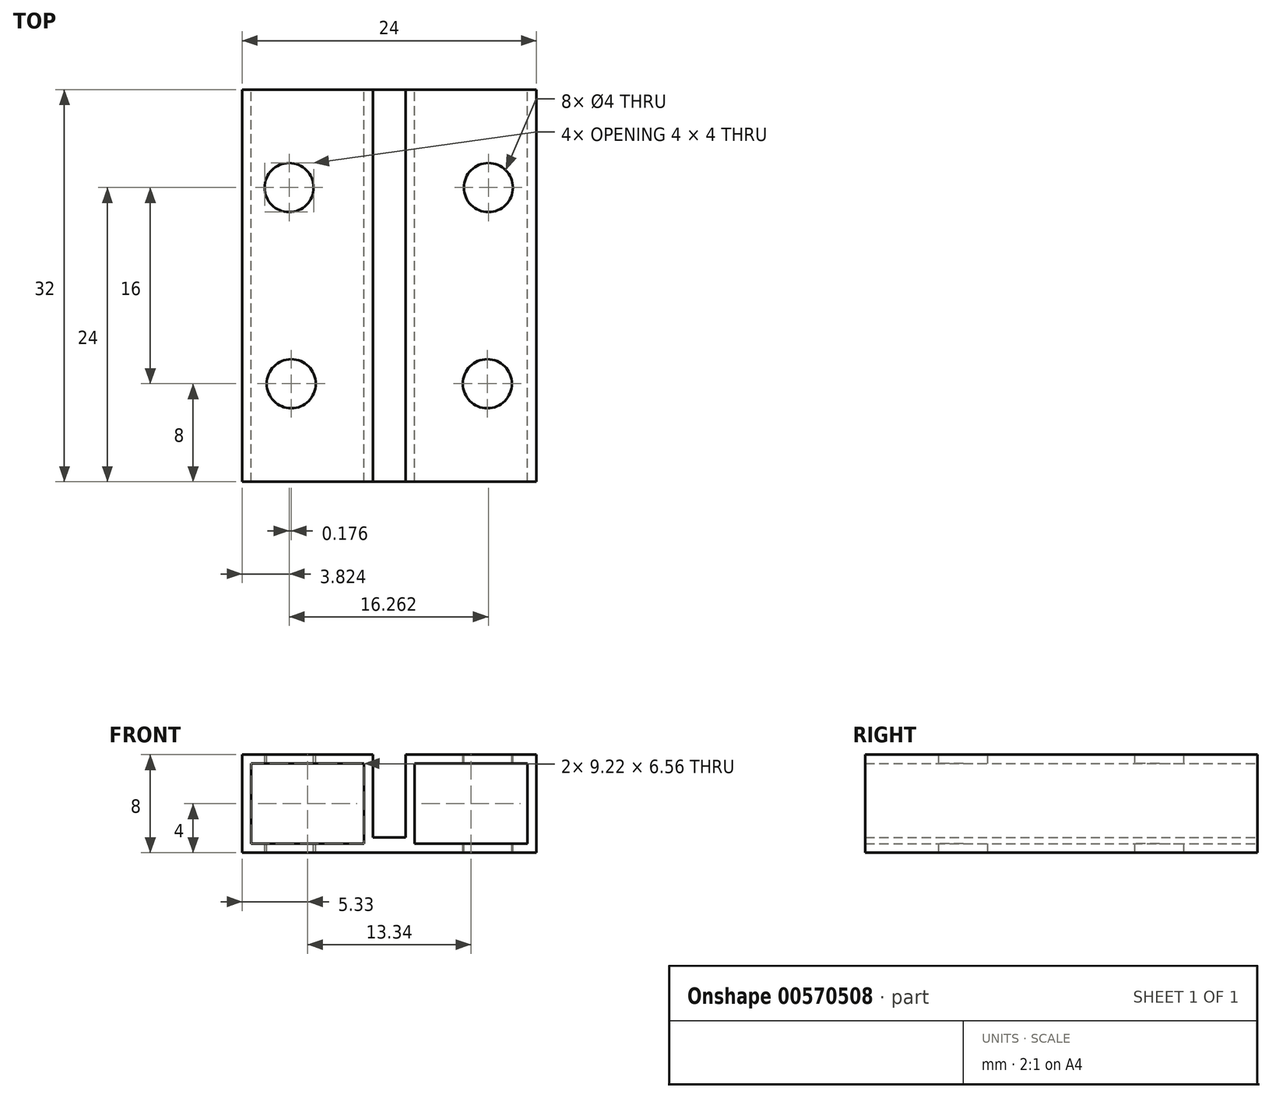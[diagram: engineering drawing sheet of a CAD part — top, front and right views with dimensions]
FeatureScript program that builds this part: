
annotation { "Feature Type Name" : "Feature", "Feature Type Description" : "" }
export const myFeature = defineFeature(function(context is Context, id is Id, definition is map)
    precondition{}
    {
        {
            var Q0;
            Q0=qCreatedBy(makeId("Front.planeOp"),FACE);
            var sketch = newSketch(context, id + "F0", { "sketchPlane" : qUnion([Q0])});
            skLineSegment(sketch, "E0.bottom", {"start": v(-12, 4) * mm, "end": v(12, 4) * mm});
            skLineSegment(sketch, "E0.top", {"start": v(-12, -4) * mm, "end": v(12, -4) * mm});
            skLineSegment(sketch, "E0.left", {"start": v(-12, 4) * mm, "end": v(-12, -4) * mm});
            skLineSegment(sketch, "E0.right", {"start": v(12, 4) * mm, "end": v(12, -4) * mm});
            skPoint(sketch, "E0.middle", {"position": v(0, 0) * mm});
            skLineSegment(sketch, "E1.bottom", {"start": v(-1.34, 10.75) * mm, "end": v(1.34, 10.75) * mm});
            skLineSegment(sketch, "E1.top", {"start": v(-1.34, -2.75) * mm, "end": v(1.34, -2.75) * mm});
            skLineSegment(sketch, "E1.left", {"start": v(-1.34, 10.75) * mm, "end": v(-1.34, -2.75) * mm});
            skLineSegment(sketch, "E1.right", {"start": v(1.34, 10.75) * mm, "end": v(1.34, -2.75) * mm});
            skPoint(sketch, "E1.middle", {"position": v(0, 4) * mm});
            skLineSegment(sketch, "E2.bottom", {"start": v(11.28, -3.28) * mm, "end": v(2.06, -3.28) * mm});
            skLineSegment(sketch, "E2.top", {"start": v(11.28, 3.28) * mm, "end": v(2.06, 3.28) * mm});
            skLineSegment(sketch, "E2.left", {"start": v(11.28, -3.28) * mm, "end": v(11.28, 3.28) * mm});
            skLineSegment(sketch, "E2.right", {"start": v(2.06, -3.28) * mm, "end": v(2.06, 3.28) * mm});
            skLineSegment(sketch, "E3.bottom", {"start": v(-2.06, 3.28) * mm, "end": v(-11.28, 3.28) * mm});
            skLineSegment(sketch, "E3.top", {"start": v(-2.06, -3.28) * mm, "end": v(-11.28, -3.28) * mm});
            skLineSegment(sketch, "E3.left", {"start": v(-2.06, 3.28) * mm, "end": v(-2.06, -3.28) * mm});
            skLineSegment(sketch, "E3.right", {"start": v(-11.28, 3.28) * mm, "end": v(-11.28, -3.28) * mm});
            skLineSegment(sketch, "E4.bottom", {"start": v(-9.78, 3.28) * mm, "end": v(-6.31, 3.28) * mm});
            skLineSegment(sketch, "E4.top", {"start": v(-9.78, -3.28) * mm, "end": v(-6.31, -3.28) * mm});
            skLineSegment(sketch, "E4.left", {"start": v(-9.78, 3.28) * mm, "end": v(-9.78, -3.28) * mm});
            skLineSegment(sketch, "E4.right", {"start": v(-6.31, 3.28) * mm, "end": v(-6.31, -3.28) * mm});
            skLineSegment(sketch, "E5.bottom", {"start": v(6.31, 3.28) * mm, "end": v(9.78, 3.28) * mm});
            skLineSegment(sketch, "E5.top", {"start": v(6.31, -3.28) * mm, "end": v(9.78, -3.28) * mm});
            skLineSegment(sketch, "E5.left", {"start": v(6.31, 3.28) * mm, "end": v(6.31, -3.28) * mm});
            skLineSegment(sketch, "E5.right", {"start": v(9.78, 3.28) * mm, "end": v(9.78, -3.28) * mm});
            skCircle(sketch, "E6", {"center": v(-8, 0) * mm, "radius": 2.16 * mm});
            skCircle(sketch, "E7", {"center": v(8, 0) * mm, "radius": 2.16 * mm});
            skSolve(sketch);
        }
        {
            var Q0;
            Q0=makeQuery(id+"F0.imprint","IMPRINT",FACE,{"disambiguationData":[TD([[makeQuery(id+"F0.imprint","IMPRINT",EDGE,{"derivedFrom":sQuery(id+"F0.wireOp",EDGE,"E0.top")}),1.0]])]});
            var Q1;
            {var subQ0=sQuery(id+"F0.wireOp",EDGE,"E4.bottom");Q1=makeQuery(id+"F0.imprint","IMPRINT",FACE,{"disambiguationData":[TD([[makeQuery(id+"F0.imprint","IMPRINT",EDGE,{"derivedFrom":subQ0}),-1.0]])]});}
            var Q2;
            {var subQ0=sQuery(id+"F0.wireOp",EDGE,"E4.top");Q2=makeQuery(id+"F0.imprint","IMPRINT",FACE,{"disambiguationData":[TD([[makeQuery(id+"F0.imprint","IMPRINT",EDGE,{"derivedFrom":subQ0}),1.0]])]});}
            var Q3;
            {var subQ0=sQuery(id+"F0.wireOp",EDGE,"E5.bottom");Q3=makeQuery(id+"F0.imprint","IMPRINT",FACE,{"disambiguationData":[TD([[makeQuery(id+"F0.imprint","IMPRINT",EDGE,{"derivedFrom":subQ0}),-1.0]])]});}
            var Q4;
            {var subQ0=sQuery(id+"F0.wireOp",EDGE,"E5.top");Q4=makeQuery(id+"F0.imprint","IMPRINT",FACE,{"disambiguationData":[TD([[makeQuery(id+"F0.imprint","IMPRINT",EDGE,{"derivedFrom":subQ0}),1.0]])]});}
            extrude(context, id + "F1", {"entities" : qUnion([Q0, Q1, Q2, Q3, Q4]), "depth" : 32 * mm, "offsetDistance" : 25 * mm});
        }
        {
            var Q0;
            {var subQ0=sQuery(id+"F0.wireOp",EDGE,"E0.bottom");Q0=makeQuery(id+"F1.opExtrude","SWEPT_FACE",FACE,{"disambiguationData":[OSD([subQ0]),TDD([makeQuery(id+"F0.imprint","IMPRINT",EDGE,{"disambiguationData":[TD([[makeQuery(id+"F0.imprint","INTERSECT",VERTEX,{"derivedFrom":[subQ0,sQuery(id+"F0.wireOp",EDGE,"E0.right")]}),1.0]])],"derivedFrom":subQ0})])]});}
            var sketch = newSketch(context, id + "F2", { "sketchPlane" : qUnion([Q0])});
            skCircle(sketch, "E8", {"center": v(8, -24) * mm, "radius": 2 * mm});
            skCircle(sketch, "E9", {"center": v(-8, -24) * mm, "radius": 2 * mm});
            skCircle(sketch, "E10", {"center": v(8.09, -8) * mm, "radius": 2 * mm});
            skCircle(sketch, "E11", {"center": v(-8.18, -8) * mm, "radius": 2 * mm});
            skSolve(sketch);
        }
        {
            var Q0;
            Q0=makeQuery(id+"F2.imprint","IMPRINT",FACE,{"disambiguationData":[TD([[makeQuery(id+"F2.imprint","IMPRINT",EDGE,{"derivedFrom":sQuery(id+"F2.wireOp",EDGE,"E9")}),1.0]])]});
            var Q1;
            Q1=makeQuery(id+"F2.imprint","IMPRINT",FACE,{"disambiguationData":[TD([[makeQuery(id+"F2.imprint","IMPRINT",EDGE,{"derivedFrom":sQuery(id+"F2.wireOp",EDGE,"E8")}),1.0]])]});
            var Q2;
            Q2=makeQuery(id+"F2.imprint","IMPRINT",FACE,{"disambiguationData":[TD([[makeQuery(id+"F2.imprint","IMPRINT",EDGE,{"derivedFrom":sQuery(id+"F2.wireOp",EDGE,"E11")}),1.0]])]});
            var Q3;
            Q3=makeQuery(id+"F2.imprint","IMPRINT",FACE,{"disambiguationData":[TD([[makeQuery(id+"F2.imprint","IMPRINT",EDGE,{"derivedFrom":sQuery(id+"F2.wireOp",EDGE,"E10")}),1.0]])]});
            extrude(context, id + "F3", {"entities" : qUnion([Q0, Q1, Q2, Q3]), "operationType" : NewBodyOperationType.REMOVE, "oppositeDirection" : true, "depth" : 8.1 * mm, "offsetDistance" : 25 * mm});
        }
    });
